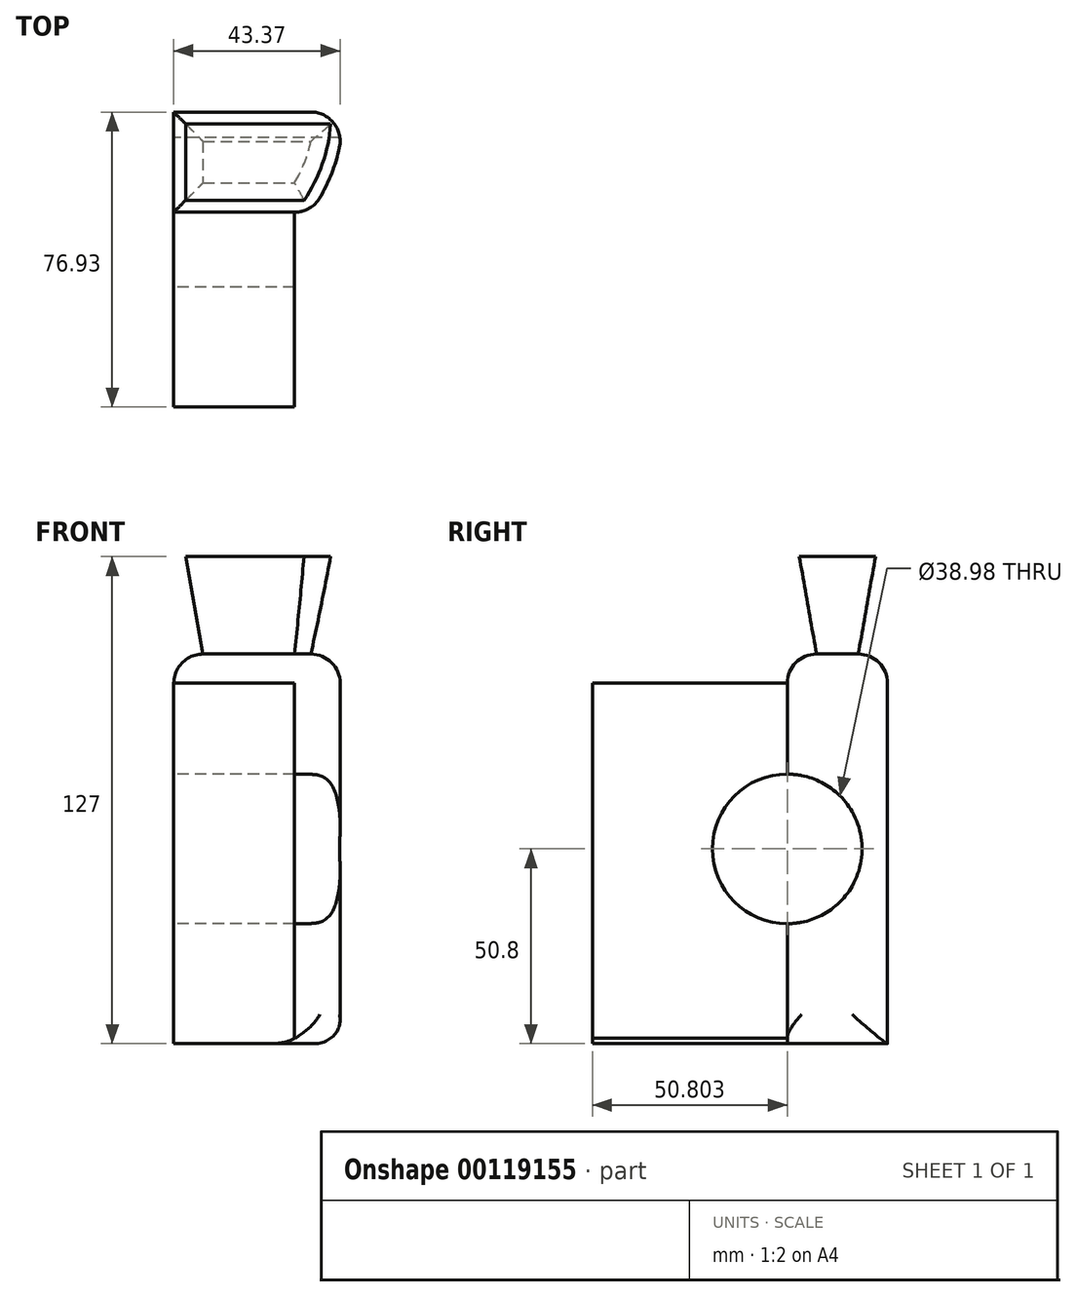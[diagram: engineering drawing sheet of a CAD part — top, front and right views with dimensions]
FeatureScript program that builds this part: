
annotation { "Feature Type Name" : "Feature", "Feature Type Description" : "" }
export const myFeature = defineFeature(function(context is Context, id is Id, definition is map)
    precondition{}
    {
        {
            var Q0;
            Q0=qCreatedBy(makeId("Top.planeOp"),FACE);
            var sketch = newSketch(context, id + "F0", { "sketchPlane" : qUnion([Q0])});
            skCircle(sketch, "E0", {"center": v(0, 0) * mm, "radius": 44.17 * mm});
            skLineSegment(sketch, "E1.bottom", {"start": v(0, 0) * mm, "end": v(92.81, 0) * mm});
            skLineSegment(sketch, "E1.top", {"start": v(0, -26.13) * mm, "end": v(92.81, -26.13) * mm});
            skLineSegment(sketch, "E1.left", {"start": v(0, 0) * mm, "end": v(0, -26.13) * mm});
            skLineSegment(sketch, "E1.right", {"start": v(92.81, 0) * mm, "end": v(92.81, -26.13) * mm});
            skSolve(sketch);
        }
        {
            var Q0;
            {var subQ5=sQuery(id+"F0.wireOp",EDGE,"E1.left");Q0=makeQuery(id+"F0.imprint","IMPRINT",FACE,{"disambiguationData":[TD([[makeQuery(id+"F0.imprint","IMPRINT",EDGE,{"derivedFrom":subQ5}),1.0]])]});}
            extrude(context, id + "F1", {"entities" : qUnion([Q0]), "depth" : 50.8 * mm, "hasSecondDirection" : true, "secondDirectionOppositeDirection" : true, "secondDirectionDepth" : 50.8 * mm});
        }
        {
            var Q0;
            Q0=makeQuery(id+"F1.opExtrude","SWEPT_FACE",FACE,{"disambiguationData":[OSD([sQuery(id+"F0.wireOp",EDGE,"E0")])]});
            var Q1;
            Q1=makeQuery(id+"F1.opExtrude","CAP_EDGE",EDGE,{"disambiguationData":[OSD([sQuery(id+"F0.wireOp",EDGE,"E0")])],"isStart":false});
            var Q2;
            Q2=makeQuery(id+"F1.opExtrude","CAP_EDGE",EDGE,{"disambiguationData":[OSD([sQuery(id+"F0.wireOp",EDGE,"E1.top")])],"isStart":false});
            var Q3;
            Q3=makeQuery(id+"F1.opExtrude","CAP_EDGE",EDGE,{"disambiguationData":[OSD([sQuery(id+"F0.wireOp",EDGE,"E1.left")])],"isStart":false});
            var Q4;
            Q4=makeQuery(id+"F1.opExtrude","CAP_EDGE",EDGE,{"disambiguationData":[OSD([sQuery(id+"F0.wireOp",EDGE,"E1.bottom")])],"isStart":false});
            fillet(context, id + "F2", {"entities" : qUnion([Q0, Q1, Q2, Q3, Q4]), "radius" : 7.62 * mm, "tangentPropagation" : true, "allowEdgeOverflow" : false});
        }
        {
            var Q0;
            Q0=makeQuery(id+"F1.opExtrude","SWEPT_FACE",FACE,{"disambiguationData":[OSD([sQuery(id+"F0.wireOp",EDGE,"E1.top")])]});
            extrude(context, id + "F3", {"entities" : qUnion([Q0]), "operationType" : NewBodyOperationType.ADD, "depth" : 50.8 * mm});
        }
        {
            var Q0;
            Q0=makeQuery(id+"F1.opExtrude","CAP_FACE",FACE,{"disambiguationData":[OSD([sQuery(id+"F0.wireOp",EDGE,"E0"),sQuery(id+"F0.wireOp",EDGE,"E1.bottom"),sQuery(id+"F0.wireOp",EDGE,"E1.top"),sQuery(id+"F0.wireOp",EDGE,"E1.left")])],"isStart":false});
            extrude(context, id + "F4", {"entities" : qUnion([Q0]), "operationType" : NewBodyOperationType.ADD, "depth" : 25.4 * mm, "hasDraft" : true, "draftAngle" : 10 * degree});
        }
        {
            var Q0;
            {var subQ0=sQuery(id+"F0.wireOp",EDGE,"E1.left");Q0=makeQuery(id+"F3.boolean.opBoolean","MERGE",FACE,{"derivedFrom":[makeQuery(id+"F1.opExtrude","SWEPT_FACE",FACE,{"disambiguationData":[OSD([subQ0])]}),makeQuery(id+"F3.opExtrude","SWEPT_FACE",FACE,{"disambiguationData":[OSD([sQuery(id+"F0.wireOp",EDGE,"E1.top"),subQ0])]})]});}
            var sketch = newSketch(context, id + "F5", { "sketchPlane" : qUnion([Q0])});
            skCircle(sketch, "E2", {"center": v(26.13, 0) * mm, "radius": 19.49 * mm});
            skSolve(sketch);
        }
        {
            var Q0;
            Q0=makeQuery(id+"F5.imprint","IMPRINT",FACE,{"disambiguationData":[TD([[makeQuery(id+"F5.imprint","IMPRINT",EDGE,{"derivedFrom":sQuery(id+"F5.wireOp",EDGE,"E2")}),1.0]])]});
            extrude(context, id + "F6", {"entities" : qUnion([Q0]), "operationType" : NewBodyOperationType.REMOVE, "oppositeDirection" : true, "depth" : 106.68 * mm, "offsetDistance" : 25.4 * mm});
        }
    });
